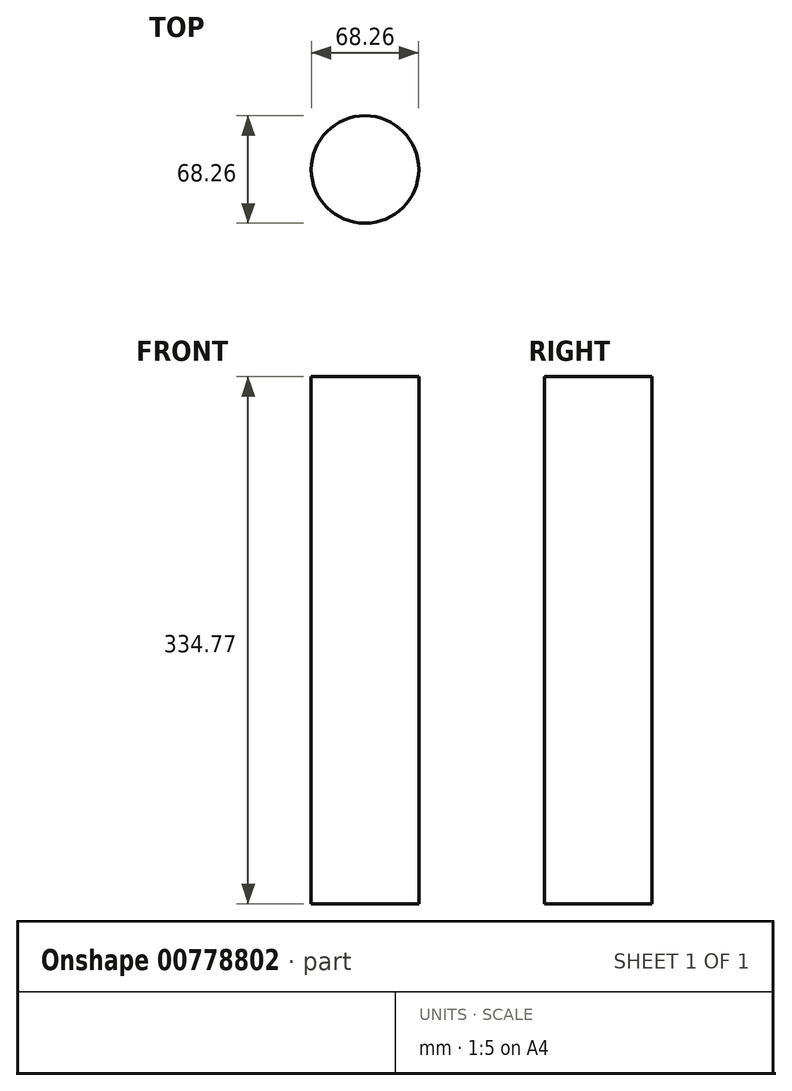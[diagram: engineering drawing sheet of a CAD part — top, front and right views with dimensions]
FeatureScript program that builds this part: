
annotation { "Feature Type Name" : "Feature", "Feature Type Description" : "" }
export const myFeature = defineFeature(function(context is Context, id is Id, definition is map)
    precondition{}
    {
        {
            var Q0;
            Q0=qCreatedBy(makeId("Top.planeOp"),FACE);
            var sketch = newSketch(context, id + "F0", { "sketchPlane" : qUnion([Q0])});
            skCircle(sketch, "E0", {"center": v(0, 0) * mm, "radius": 34.13 * mm});
            skSolve(sketch);
        }
        {
            var Q0;
            Q0=makeQuery(id+"F0.imprint","IMPRINT",FACE,{"disambiguationData":[TD([[makeQuery(id+"F0.imprint","IMPRINT",EDGE,{"derivedFrom":sQuery(id+"F0.wireOp",EDGE,"E0")}),1.0]])]});
            extrude(context, id + "F1", {"entities" : qUnion([Q0]), "depth" : 334.77 * mm, "offsetDistance" : 25.4 * mm});
        }
    });
